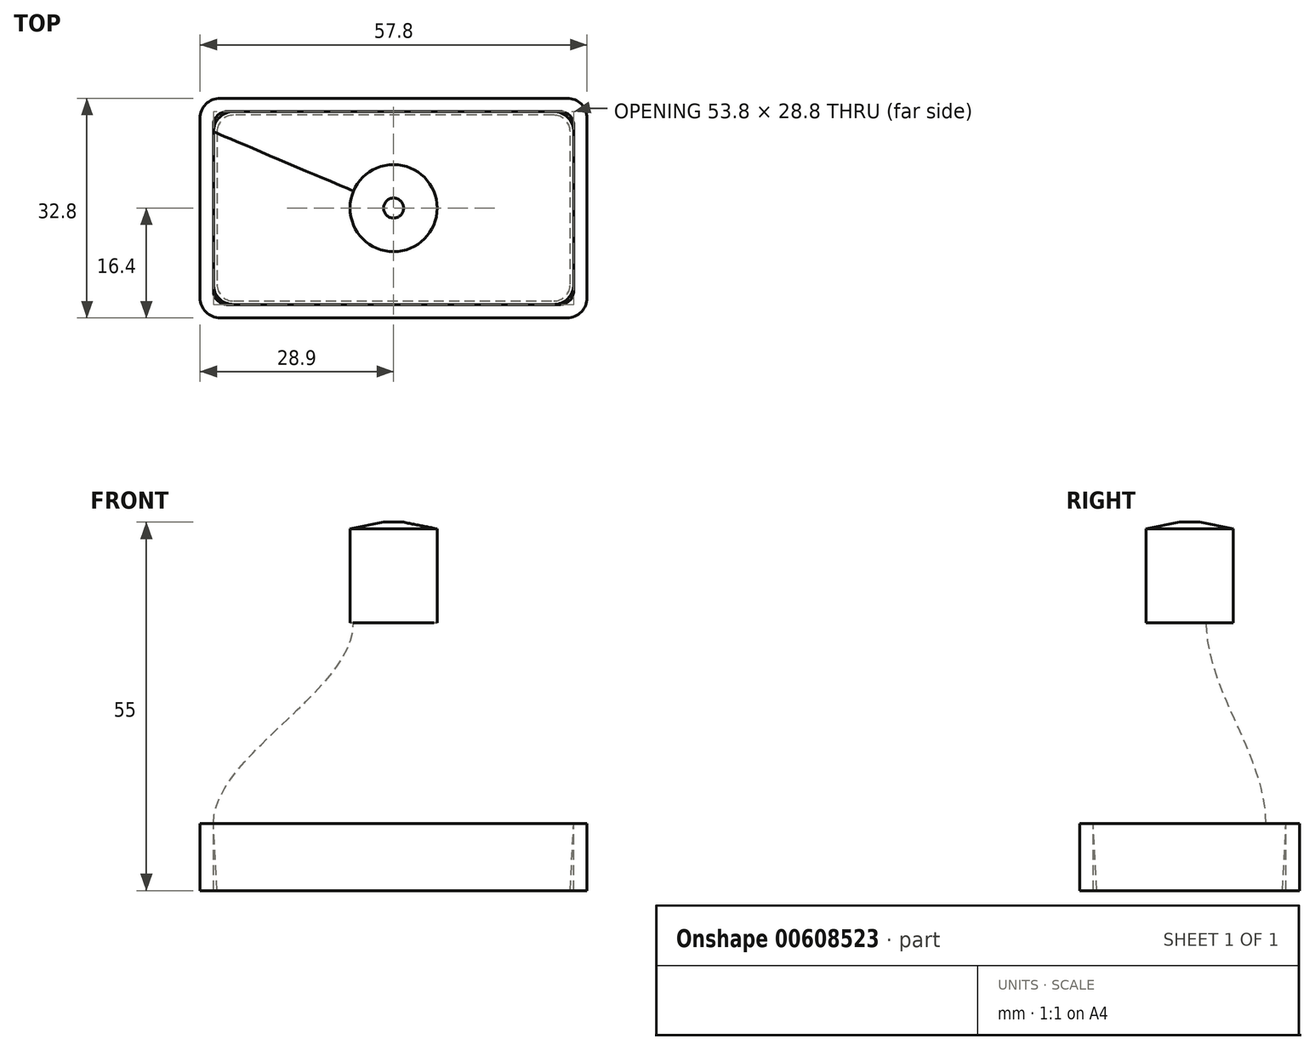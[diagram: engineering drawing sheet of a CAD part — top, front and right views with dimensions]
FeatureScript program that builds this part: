
annotation { "Feature Type Name" : "Feature", "Feature Type Description" : "" }
export const myFeature = defineFeature(function(context is Context, id is Id, definition is map)
    precondition{}
    {
        {
            var Q0;
            Q0=qCreatedBy(makeId("Top.planeOp"),FACE);
            var sketch = newSketch(context, id + "F0", { "sketchPlane" : qUnion([Q0])});
            skLineSegment(sketch, "E0", {"start": v(-75.7, 0) * mm, "end": v(75.36, 0) * mm, "construction": true});
            skLineSegment(sketch, "E1", {"start": v(0, 75.7) * mm, "end": v(0, -73.25) * mm, "construction": true});
            skSolve(sketch);
        }
        {
            var Q0;
            Q0=qCreatedBy(makeId("Top.planeOp"),FACE);
            var sketch = newSketch(context, id + "F1", { "sketchPlane" : qUnion([Q0])});
            skLineSegment(sketch, "E2.bottom", {"start": v(25.9, 16.4) * mm, "end": v(-25.9, 16.4) * mm});
            skLineSegment(sketch, "E2.top", {"start": v(25.9, -16.4) * mm, "end": v(-25.9, -16.4) * mm});
            skLineSegment(sketch, "E2.left", {"start": v(28.9, 13.4) * mm, "end": v(28.9, -13.4) * mm});
            skLineSegment(sketch, "E2.right", {"start": v(-28.9, 13.4) * mm, "end": v(-28.9, -13.4) * mm});
            skPoint(sketch, "E2.middle", {"position": v(0, 0) * mm});
            skLineSegment(sketch, "E3.0", {"start": v(24.9, 14.4) * mm, "end": v(-24.9, 14.4) * mm});
            skLineSegment(sketch, "E3.1", {"start": v(26.9, 12.4) * mm, "end": v(26.9, -12.4) * mm});
            skLineSegment(sketch, "E3.2", {"start": v(24.9, -14.4) * mm, "end": v(-24.9, -14.4) * mm});
            skLineSegment(sketch, "E3.3", {"start": v(-26.9, 12.4) * mm, "end": v(-26.9, -12.4) * mm});
            skPoint(sketch, "E4.visualSharp", {"position": v(28.9, 16.4) * mm});
            skArc(sketch, "E4.filletArc", {"start": v(28.9, 13.4) * mm, "mid": v(28.02, 15.52) * mm, "end": v(25.9, 16.4) * mm});
            skPoint(sketch, "E5.visualSharp", {"position": v(-28.9, 16.4) * mm});
            skArc(sketch, "E5.filletArc", {"start": v(-25.9, 16.4) * mm, "mid": v(-28.02, 15.52) * mm, "end": v(-28.9, 13.4) * mm});
            skPoint(sketch, "E6.visualSharp", {"position": v(-28.9, -16.4) * mm});
            skArc(sketch, "E6.filletArc", {"start": v(-28.9, -13.4) * mm, "mid": v(-28.02, -15.52) * mm, "end": v(-25.9, -16.4) * mm});
            skPoint(sketch, "E7.visualSharp", {"position": v(28.9, -16.4) * mm});
            skArc(sketch, "E7.filletArc", {"start": v(25.9, -16.4) * mm, "mid": v(28.02, -15.52) * mm, "end": v(28.9, -13.4) * mm});
            skPoint(sketch, "E8.visualSharp", {"position": v(26.9, 14.4) * mm});
            skArc(sketch, "E8.filletArc", {"start": v(26.9, 12.4) * mm, "mid": v(26.31, 13.81) * mm, "end": v(24.9, 14.4) * mm});
            skPoint(sketch, "E9.visualSharp", {"position": v(-26.9, 14.4) * mm});
            skArc(sketch, "E9.filletArc", {"start": v(-24.9, 14.4) * mm, "mid": v(-26.31, 13.81) * mm, "end": v(-26.9, 12.4) * mm});
            skPoint(sketch, "E10.visualSharp", {"position": v(-26.9, -14.4) * mm});
            skArc(sketch, "E10.filletArc", {"start": v(-26.9, -12.4) * mm, "mid": v(-26.31, -13.81) * mm, "end": v(-24.9, -14.4) * mm});
            skPoint(sketch, "E11.visualSharp", {"position": v(26.9, -14.4) * mm});
            skArc(sketch, "E11.filletArc", {"start": v(24.9, -14.4) * mm, "mid": v(26.31, -13.81) * mm, "end": v(26.9, -12.4) * mm});
            skLineSegment(sketch, "E12", {"start": v(0, -14.4) * mm, "end": v(0, 14.4) * mm});
            skSolve(sketch);
        }
        {
            var Q0;
            Q0=makeQuery(id+"F1.imprint","IMPRINT",FACE,{"disambiguationData":[TD([[makeQuery(id+"F1.imprint","IMPRINT",EDGE,{"derivedFrom":sQuery(id+"F1.wireOp",EDGE,"E2.bottom")}),1.0]])]});
            extrude(context, id + "F2", {"entities" : qUnion([Q0]), "oppositeDirection" : true, "depth" : 10 * mm, "offsetDistance" : 25 * mm});
        }
        {
            var Q0;
            Q0=qCreatedBy(makeId("Top.planeOp"),FACE);
            cPlane(context, id + "F3", {"entities" : qUnion([Q0]), "cplaneType" : CPlaneType.OFFSET, "offset" : 30 * mm, "width" : 150 * mm, "height" : 150 * mm});
        }
        {
            var Q0;
            Q0=qCreatedBy(id+"F3.planeOp",FACE);
            var sketch = newSketch(context, id + "F4", { "sketchPlane" : qUnion([Q0])});
            skLineSegment(sketch, "E13.0.0", {"start": v(-25.9, -16.4) * mm, "end": v(25.9, -16.4) * mm, "construction": true});
            skArc(sketch, "E13.0.1", {"start": v(25.9, -16.4) * mm, "mid": v(28.02, -15.52) * mm, "end": v(28.9, -13.4) * mm, "construction": true});
            skLineSegment(sketch, "E13.0.2", {"start": v(28.9, -13.4) * mm, "end": v(28.9, 13.4) * mm, "construction": true});
            skArc(sketch, "E13.0.3", {"start": v(28.9, 13.4) * mm, "mid": v(28.02, 15.52) * mm, "end": v(25.9, 16.4) * mm, "construction": true});
            skLineSegment(sketch, "E13.0.4", {"start": v(25.9, 16.4) * mm, "end": v(-25.9, 16.4) * mm, "construction": true});
            skArc(sketch, "E13.0.5", {"start": v(-25.9, 16.4) * mm, "mid": v(-28.02, 15.52) * mm, "end": v(-28.9, 13.4) * mm, "construction": true});
            skLineSegment(sketch, "E13.0.6", {"start": v(-28.9, 13.4) * mm, "end": v(-28.9, -13.4) * mm, "construction": true});
            skArc(sketch, "E13.0.7", {"start": v(-28.9, -13.4) * mm, "mid": v(-28.02, -15.52) * mm, "end": v(-25.9, -16.4) * mm, "construction": true});
            skLineSegment(sketch, "E14.0", {"start": v(24.9, 14.4) * mm, "end": v(-24.9, 14.4) * mm, "construction": true});
            skArc(sketch, "E15.0", {"start": v(-24.9, 14.4) * mm, "mid": v(-26.31, 13.81) * mm, "end": v(-26.9, 12.4) * mm, "construction": true});
            skLineSegment(sketch, "E16.0", {"start": v(-26.9, 12.4) * mm, "end": v(-26.9, -12.4) * mm, "construction": true});
            skArc(sketch, "E17.0", {"start": v(-26.9, -12.4) * mm, "mid": v(-26.31, -13.81) * mm, "end": v(-24.9, -14.4) * mm, "construction": true});
            skLineSegment(sketch, "E18.0", {"start": v(24.9, -14.4) * mm, "end": v(-24.9, -14.4) * mm, "construction": true});
            skArc(sketch, "E19.0", {"start": v(24.9, -14.4) * mm, "mid": v(26.31, -13.81) * mm, "end": v(26.9, -12.4) * mm, "construction": true});
            skLineSegment(sketch, "E20.0", {"start": v(26.9, 12.4) * mm, "end": v(26.9, -12.4) * mm, "construction": true});
            skArc(sketch, "E21.0", {"start": v(26.9, 12.4) * mm, "mid": v(26.31, 13.81) * mm, "end": v(24.9, 14.4) * mm, "construction": true});
            skLineSegment(sketch, "E22", {"start": v(-41, 0) * mm, "end": v(-28.9, 0) * mm, "construction": true});
            skLineSegment(sketch, "E23", {"start": v(0, 27.8) * mm, "end": v(0, 16.4) * mm, "construction": true});
            skLineSegment(sketch, "E24", {"start": v(0, 0) * mm, "end": v(26.9, 0) * mm, "construction": true});
            skLineSegment(sketch, "E25", {"start": v(0, 0) * mm, "end": v(0, -14.4) * mm, "construction": true});
            skLineSegment(sketch, "E26.trimOffspring", {"start": v(-26.9, 0) * mm, "end": v(0, 0) * mm, "construction": true});
            skLineSegment(sketch, "E27.trimOffspring", {"start": v(0, 14.4) * mm, "end": v(0, 0) * mm, "construction": true});
            skLineSegment(sketch, "E28.trimOffspring", {"start": v(0, -16.4) * mm, "end": v(0, -30.82) * mm, "construction": true});
            skLineSegment(sketch, "E29.trimOffspring", {"start": v(28.9, 0) * mm, "end": v(49.7, 0) * mm, "construction": true});
            skPoint(sketch, "E30", {"position": v(-13.45, 0) * mm});
            skPoint(sketch, "E31", {"position": v(13.45, 0) * mm});
            skCircle(sketch, "E32", {"center": v(-13.45, 0) * mm, "radius": 6.5 * mm, "construction": true});
            skCircle(sketch, "E33", {"center": v(13.45, 0) * mm, "radius": 6.5 * mm, "construction": true});
            skCircle(sketch, "E34", {"center": v(0, 0) * mm, "radius": 6.5 * mm});
            skSolve(sketch);
        }
        {
            var Q0;
            Q0=qCreatedBy(makeId("Top.planeOp"),FACE);
            var sketch = newSketch(context, id + "F5", { "sketchPlane" : qUnion([Q0])});
            skLineSegment(sketch, "E35.0", {"start": v(-26.9, 11.4) * mm, "end": v(-26.9, -11.4) * mm});
            skLineSegment(sketch, "E36.0", {"start": v(23.9, 14.4) * mm, "end": v(-23.9, 14.4) * mm});
            skLineSegment(sketch, "E37.0", {"start": v(26.9, 11.4) * mm, "end": v(26.9, -11.4) * mm});
            skLineSegment(sketch, "E38.0", {"start": v(23.9, -14.4) * mm, "end": v(-23.9, -14.4) * mm});
            skPoint(sketch, "E39.visualSharp", {"position": v(-26.9, -14.4) * mm});
            skArc(sketch, "E39.filletArc", {"start": v(-26.9, -11.4) * mm, "mid": v(-26.02, -13.52) * mm, "end": v(-23.9, -14.4) * mm});
            skPoint(sketch, "E40.visualSharp", {"position": v(26.9, -14.4) * mm});
            skArc(sketch, "E40.filletArc", {"start": v(23.9, -14.4) * mm, "mid": v(26.02, -13.52) * mm, "end": v(26.9, -11.4) * mm});
            skPoint(sketch, "E41.visualSharp", {"position": v(26.9, 14.4) * mm});
            skArc(sketch, "E41.filletArc", {"start": v(26.9, 11.4) * mm, "mid": v(26.02, 13.52) * mm, "end": v(23.9, 14.4) * mm});
            skPoint(sketch, "E42.visualSharp", {"position": v(-26.9, 14.4) * mm});
            skArc(sketch, "E42.filletArc", {"start": v(-23.9, 14.4) * mm, "mid": v(-26.02, 13.52) * mm, "end": v(-26.9, 11.4) * mm});
            skSolve(sketch);
        }
        {
            var Q0;
            Q0=makeQuery(id+"F5.imprint","IMPRINT",FACE,{"disambiguationData":[TD([[makeQuery(id+"F5.imprint","IMPRINT",EDGE,{"derivedFrom":sQuery(id+"F5.wireOp",EDGE,"E35.0")}),1.0]])]});
            var Q1;
            Q1=makeQuery(id+"F4.imprint","IMPRINT",FACE,{"disambiguationData":[TD([[makeQuery(id+"F4.imprint","IMPRINT",EDGE,{"derivedFrom":sQuery(id+"F4.wireOp",EDGE,"E34")}),1.0]])]});
            loft(context, id + "F6", {"startCondition" : LoftEndDerivativeType.NORMAL_TO_PROFILE, "startMagnitude" : 1, "endCondition" : LoftEndDerivativeType.NORMAL_TO_PROFILE, "endMagnitude" : 1, "sheetProfilesArray" : [{ "sheetProfileEntities" : qUnion([Q0]) }, { "sheetProfileEntities" : qUnion([Q1]) }]});
        }
        {
            var Q0;
            Q0=makeQuery(id+"F4.imprint","IMPRINT",FACE,{"disambiguationData":[TD([[makeQuery(id+"F4.imprint","IMPRINT",EDGE,{"derivedFrom":sQuery(id+"F4.wireOp",EDGE,"E34")}),1.0]])]});
            extrude(context, id + "F7", {"entities" : qUnion([Q0]), "depth" : 15 * mm, "offsetDistance" : 25 * mm});
        }
        {
            var Q0;
            Q0=makeQuery(id+"F7.opExtrude","CAP_FACE",FACE,{"disambiguationData":[OSD([sQuery(id+"F4.wireOp",EDGE,"E32")])],"isStart":false});
            var Q1;
            Q1=makeQuery(id+"F7.opExtrude","CAP_FACE",FACE,{"disambiguationData":[OSD([sQuery(id+"F4.wireOp",EDGE,"E33")])],"isStart":false});
            var Q2;
            Q2=makeQuery(id+"F7.opExtrude","CAP_EDGE",EDGE,{"disambiguationData":[OSD([sQuery(id+"F4.wireOp",EDGE,"E34")])],"isStart":false});
            chamfer(context, id + "F8", {"entities" : qUnion([Q0, Q1, Q2]), "chamferType" : ChamferType.TWO_OFFSETS, "width1" : 1 * mm, "oppositeDirection" : false, "width2" : 5 * mm, "tangentPropagation" : true});
        }
        {
            var Q0;
            Q0=makeQuery(id+"F5.imprint","IMPRINT",FACE,{"disambiguationData":[TD([[makeQuery(id+"F5.imprint","IMPRINT",EDGE,{"derivedFrom":sQuery(id+"F5.wireOp",EDGE,"E35.0")}),1.0]])]});
            var Q1;
            Q1=makeQuery(id+"F2.opExtrude","CAP_FACE",FACE,{"disambiguationData":[OSD([sQuery(id+"F1.wireOp",EDGE,"E2.bottom"),sQuery(id+"F1.wireOp",EDGE,"E2.top"),sQuery(id+"F1.wireOp",EDGE,"E2.left"),sQuery(id+"F1.wireOp",EDGE,"E2.right"),sQuery(id+"F1.wireOp",EDGE,"E3.0"),sQuery(id+"F1.wireOp",EDGE,"E3.1"),sQuery(id+"F1.wireOp",EDGE,"E3.2"),sQuery(id+"F1.wireOp",EDGE,"E3.3"),sQuery(id+"F1.wireOp",EDGE,"E4.filletArc"),sQuery(id+"F1.wireOp",EDGE,"E5.filletArc"),sQuery(id+"F1.wireOp",EDGE,"E6.filletArc"),sQuery(id+"F1.wireOp",EDGE,"E7.filletArc"),sQuery(id+"F1.wireOp",EDGE,"E8.filletArc"),sQuery(id+"F1.wireOp",EDGE,"E9.filletArc"),sQuery(id+"F1.wireOp",EDGE,"E10.filletArc"),sQuery(id+"F1.wireOp",EDGE,"E11.filletArc")])],"isStart":false});
            extrude(context, id + "F9", {"entities" : qUnion([Q0]), "oppositeDirection" : true, "depth" : 10 * mm, "endBoundEntityFace" : qUnion([Q1]), "offsetDistance" : 25 * mm, "hasDraft" : true, "draftAngle" : 3 * degree, "draftPullDirection" : true});
        }
    });
